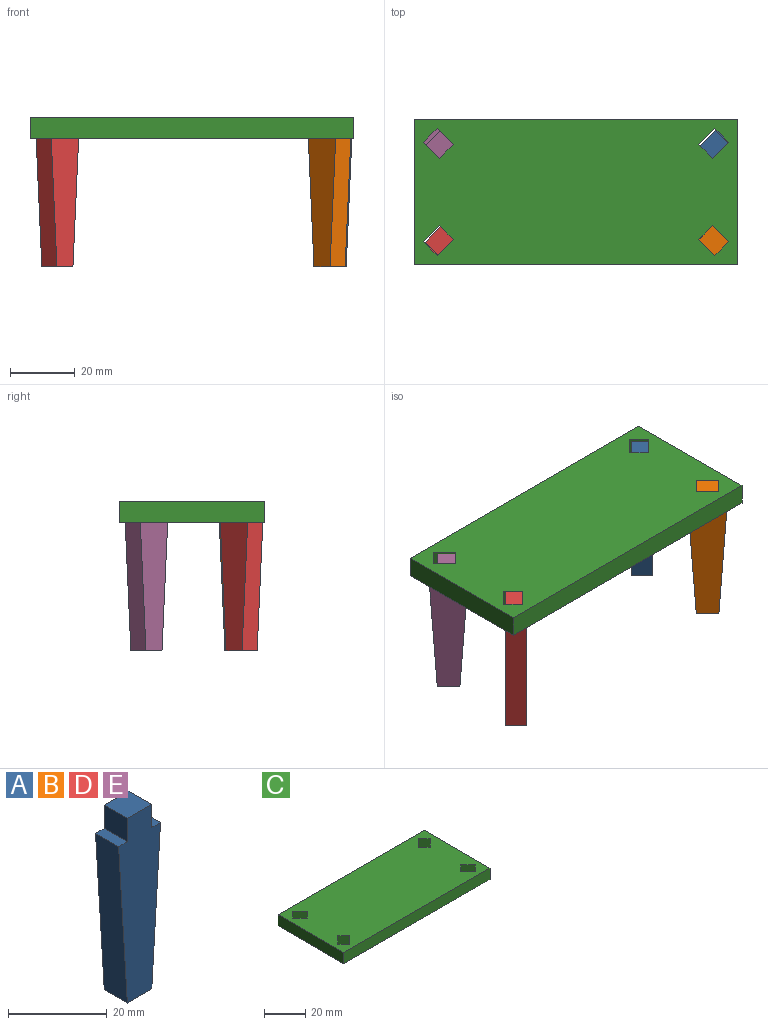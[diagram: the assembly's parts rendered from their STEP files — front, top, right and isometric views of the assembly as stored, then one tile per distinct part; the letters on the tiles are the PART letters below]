
ASSEMBLY  parts=5 mates=1
PART A: 10 faces, bbox 12x6.6x45.8 mm
  f0: plane 7x6.6mm, normal (0,0,1), area 46.2mm2, adj f1,f7,f8,f9
  f1: plane 6.6x5.78mm, normal (-1,0,0), area 38.1mm2, adj f0,f2,f8,f9
  f2: plane 6.6x2.5mm, normal (0,0,1), area 16.5mm2, adj f1,f3,f8,f9
  f3: plane 40x6.6mm, normal (-1,0,-0.06), area 264.5mm2, adj f2,f4,f8,f9
  f4: plane 7x6.6mm, normal (0,0,-1), area 46.2mm2, adj f3,f5,f8,f9
  f5: plane 40x6.6mm, normal (1,0,-0.06), area 264.5mm2, adj f4,f6,f8,f9
  f6: plane 6.6x2.5mm, normal (0,0,1), area 16.5mm2, adj f5,f7,f8,f9
  f7: plane 6.6x5.78mm, normal (1,0,0), area 38.1mm2, adj f0,f6,f8,f9
  f8: plane 45.78x12mm, normal (0,-1,0), area 420.5mm2, adj f0,f1,f2,f3,f4,f5,f6,f7
  f9: plane 45.78x12mm, normal (0,1,0), area 420.5mm2, adj f0,f1,f2,f3,f4,f5,f6,f7
PART B: same geometry as A
PART C: 22 faces, bbox 100x45x6.6 mm
  f0: plane 6.6x4.95mm, normal (-0.71,0.71,0), area 46.2mm2, adj f1,f19,f20,f21
  f1: plane 6.6x4.09mm, normal (0.71,0.71,0), area 38.1mm2, adj f0,f2,f20,f21
  f2: plane 6.6x4.95mm, normal (0.71,-0.71,0), area 46.2mm2, adj f1,f19,f20,f21
  f3: plane 6.6x4.95mm, normal (0.71,-0.71,0), area 46.2mm2, adj f4,f15,f20,f21
  f4: plane 6.6x4.09mm, normal (-0.71,-0.71,0), area 38.1mm2, adj f3,f5,f20,f21
  f5: plane 6.6x4.95mm, normal (-0.71,0.71,0), area 46.2mm2, adj f4,f15,f20,f21
  f6: plane 6.6x4.95mm, normal (0.71,0.71,0), area 46.2mm2, adj f7,f16,f20,f21
  f7: plane 6.6x4.09mm, normal (0.71,-0.71,0), area 38.1mm2, adj f6,f8,f20,f21
  f8: plane 6.6x4.95mm, normal (-0.71,-0.71,0), area 46.2mm2, adj f7,f16,f20,f21
  f9: plane 6.6x4.95mm, normal (-0.71,-0.71,0), area 46.2mm2, adj f10,f17,f20,f21
  f10: plane 6.6x4.09mm, normal (-0.71,0.71,0), area 38.1mm2, adj f9,f11,f20,f21
  f11: plane 6.6x4.95mm, normal (0.71,0.71,0), area 46.2mm2, adj f10,f17,f20,f21
  f12: plane 45x6.6mm, normal (1,0,0), area 297mm2, adj f13,f18,f20,f21
  f13: plane 100x6.6mm, normal (0,1,0), area 660mm2, adj f12,f14,f20,f21
  f14: plane 45x6.6mm, normal (-1,0,0), area 297mm2, adj f13,f18,f20,f21
  f15: plane 6.6x4.09mm, normal (0.71,0.71,0), area 38.1mm2, adj f3,f5,f20,f21
  f16: plane 6.6x4.09mm, normal (-0.71,0.71,0), area 38.1mm2, adj f6,f8,f20,f21
  f17: plane 6.6x4.09mm, normal (0.71,-0.71,0), area 38.1mm2, adj f9,f11,f20,f21
  f18: plane 100x6.6mm, normal (0,-1,0), area 660mm2, adj f12,f14,f20,f21
  f19: plane 6.6x4.09mm, normal (-0.71,-0.71,0), area 38.1mm2, adj f0,f2,f20,f21
  f20: plane 100x45mm, normal (0,0,1), area 4338.2mm2, adj f0,f1,f2,f3,f4,f5,f6,f7
  f21: plane 100x45mm, normal (0,0,-1), area 4338.2mm2, adj f0,f1,f2,f3,f4,f5,f6,f7
PART D: same geometry as A
PART E: same geometry as A
PLACE A rot(axis=(0,0,1),45deg) t=(45.52,18.96,1.24)mm
PLACE B rot(axis=(0,0,1),135deg) t=(45.19,-14.77,1.24)mm
PLACE C t=(5.05,2.55,-2.06)mm
PLACE D rot(axis=(0,0,-1),135deg) t=(-34.2,-15.09,1.24)mm
PLACE E rot(axis=(0,0,1),135deg) t=(-38.86,14.29,1.24)mm
MATE fastened B.f7 <-> C.f17  axis (-0.71,0.71,0) through (45.05,-9.96,1.24)mm
